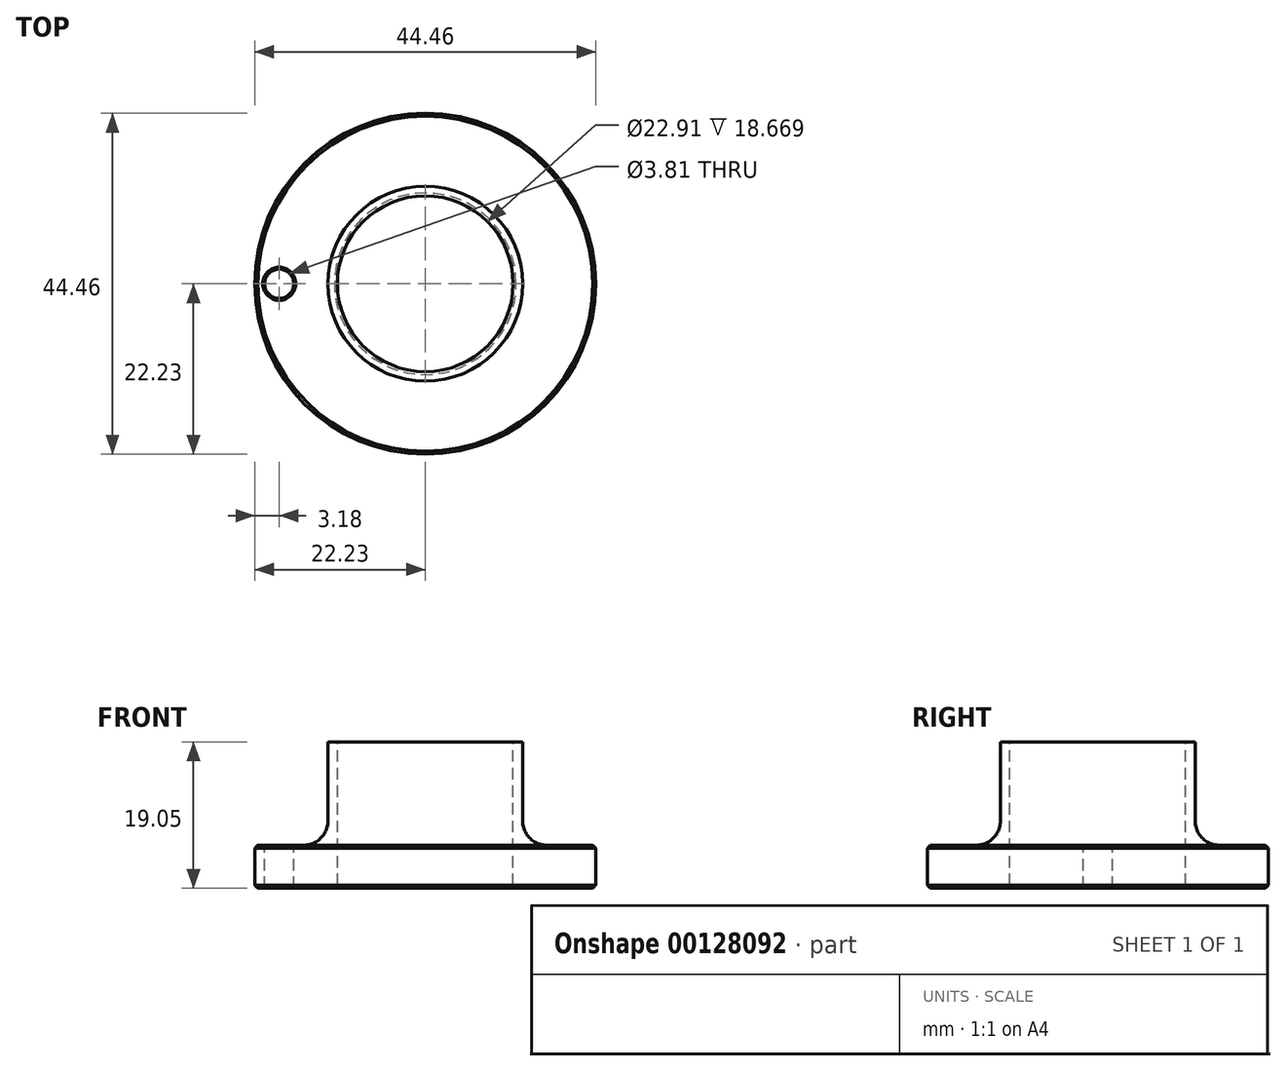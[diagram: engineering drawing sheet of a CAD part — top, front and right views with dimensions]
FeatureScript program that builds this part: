
annotation { "Feature Type Name" : "Feature", "Feature Type Description" : "" }
export const myFeature = defineFeature(function(context is Context, id is Id, definition is map)
    precondition{}
    {
        {
            var Q0;
            Q0=qCreatedBy(makeId("Front.planeOp"),FACE);
            var sketch = newSketch(context, id + "F0", { "sketchPlane" : qUnion([Q0])});
            skLineSegment(sketch, "E0", {"start": v(11.46, 19.05) * mm, "end": v(11.46, 0) * mm});
            skLineSegment(sketch, "E1", {"start": v(11.46, 0) * mm, "end": v(22.23, 0) * mm});
            skLineSegment(sketch, "E2", {"start": v(22.23, 0) * mm, "end": v(22.23, 5.59) * mm});
            skLineSegment(sketch, "E3", {"start": v(22.23, 5.59) * mm, "end": v(15.88, 5.59) * mm});
            skLineSegment(sketch, "E4", {"start": v(11.46, 19.05) * mm, "end": v(12.7, 19.05) * mm});
            skLineSegment(sketch, "E5", {"start": v(12.7, 19.05) * mm, "end": v(12.7, 8.76) * mm});
            skArc(sketch, "E6", {"start": v(12.7, 8.76) * mm, "mid": v(13.63, 6.52) * mm, "end": v(15.88, 5.59) * mm});
            skLineSegment(sketch, "E7", {"start": v(0, 0) * mm, "end": v(0, -17.58) * mm, "construction": true});
            skSolve(sketch);
        }
        {
            var Q0;
            Q0 = qSketchRegion(id + "F0", true);
            var Q1;
            Q1=sQuery(id+"F0.wireOp",EDGE,"E7");
            revolve(context, id + "F1", {"entities" : qUnion([Q0]), "axis" : qUnion([Q1]), "revolveType" : RevolveType.FULL});
        }
        {
            var Q0;
            Q0=makeQuery(id+"F1.opRevolve","SWEPT_FACE",FACE,{"disambiguationData":[OSD([sQuery(id+"F0.wireOp",EDGE,"E3")])]});
            var sketch = newSketch(context, id + "F2", { "sketchPlane" : qUnion([Q0])});
            skPoint(sketch, "E8", {"position": v(-19.05, 0) * mm});
            skCircle(sketch, "E9", {"center": v(0, 0) * mm, "radius": 19.05 * mm});
            skSolve(sketch);
        }
        {
            var Q0;
            Q0=sQuery(id+"F2.wireOp",VERTEX,"E8");
            var Q1;
            Q1=makeQuery(id+"F1.opRevolve","SWEPT_BODY",BODY,{"disambiguationData":[OSD([sQuery(id+"F0.wireOp",EDGE,"E0"),sQuery(id+"F0.wireOp",EDGE,"E1"),sQuery(id+"F0.wireOp",EDGE,"E2"),sQuery(id+"F0.wireOp",EDGE,"E3"),sQuery(id+"F0.wireOp",EDGE,"E4"),sQuery(id+"F0.wireOp",EDGE,"E5"),sQuery(id+"F0.wireOp",EDGE,"E6")])]});
            hole(context, id + "F3", {"style" : HoleStyle.C_SINK, "endStyle" : HoleEndStyle.THROUGH, "holeDiameter" : 3.8 * mm, "cSinkDiameter" : 4.32 * mm, "cSinkAngle" : 90 * degree, "locations" : qUnion([Q0]), "scope" : qUnion([Q1]), "isTappedThrough" : true});
        }
        {
            var Q0;
            Q0=makeQuery(id+"F1.opRevolve","SWEPT_EDGE",EDGE,{"disambiguationData":[OSD([sQuery(id+"F0.wireOp",EDGE,"E2"),sQuery(id+"F0.wireOp",EDGE,"E3")])]});
            var Q1;
            Q1=makeQuery(id+"F1.opRevolve","SWEPT_EDGE",EDGE,{"disambiguationData":[OSD([sQuery(id+"F0.wireOp",EDGE,"E1"),sQuery(id+"F0.wireOp",EDGE,"E2")])]});
            var Q2;
            Q2=makeQuery(id+"F1.opRevolve","SWEPT_EDGE",EDGE,{"disambiguationData":[OSD([sQuery(id+"F0.wireOp",EDGE,"E0"),sQuery(id+"F0.wireOp",EDGE,"E1")])]});
            chamfer(context, id + "F4", {"entities" : qUnion([Q0, Q1, Q2]), "chamferType" : ChamferType.OFFSET_ANGLE, "width" : 0.38 * mm, "oppositeDirection" : false, "angle" : 45 * degree, "tangentPropagation" : true});
        }
    });
